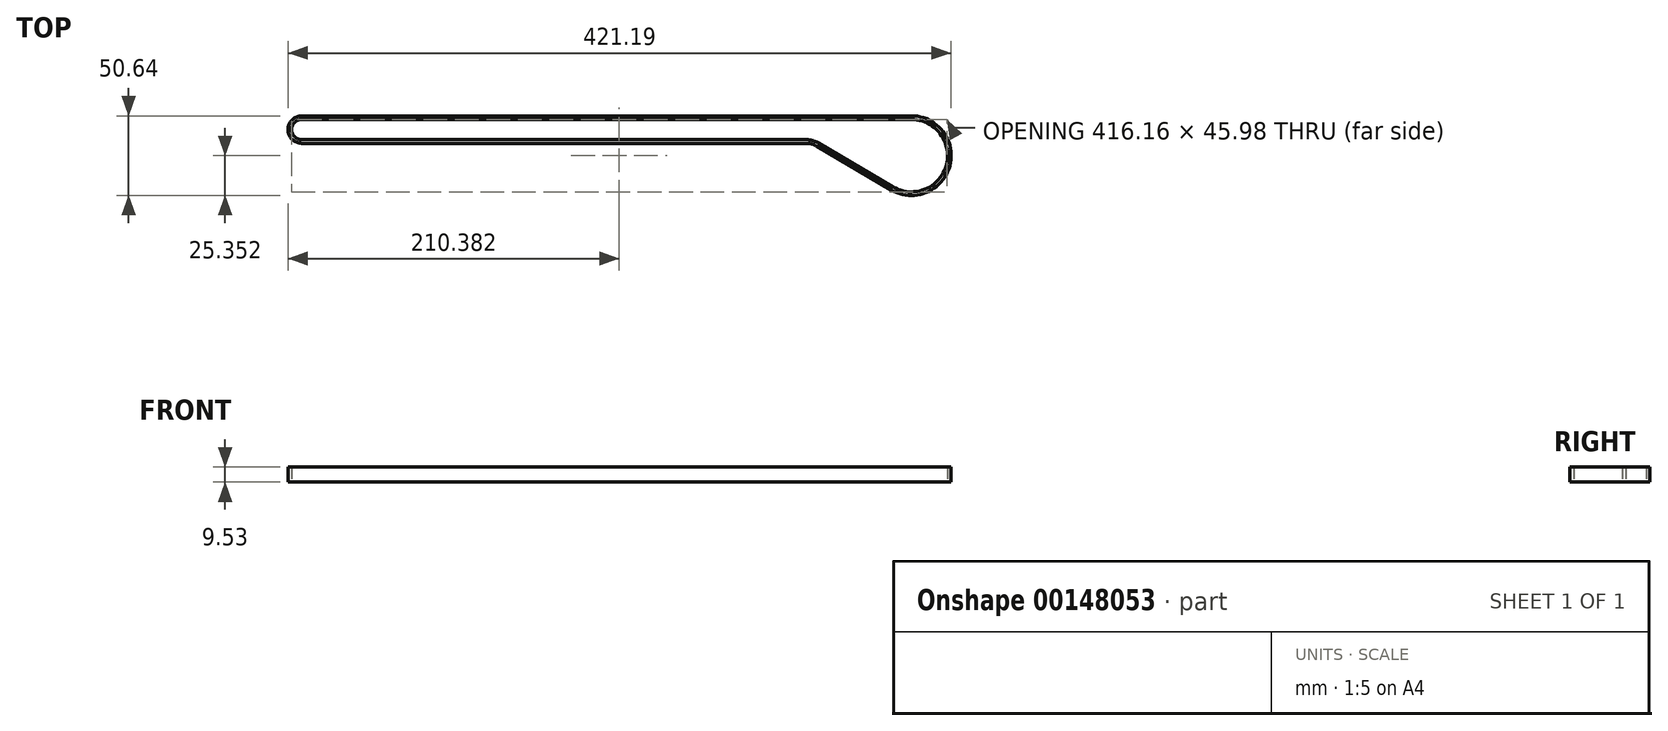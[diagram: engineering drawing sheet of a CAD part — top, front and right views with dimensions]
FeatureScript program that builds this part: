
annotation { "Feature Type Name" : "Feature", "Feature Type Description" : "" }
export const myFeature = defineFeature(function(context is Context, id is Id, definition is map)
    precondition{}
    {
        {
            var Q0;
            Q0=qCreatedBy(makeId("Top.planeOp"),FACE);
            var sketch = newSketch(context, id + "F0", { "sketchPlane" : qUnion([Q0])});
            skArc(sketch, "E0", {"start": v(-11.7, -42.85) * mm, "mid": v(22.2, -29.08) * mm, "end": v(0, 0) * mm});
            skLineSegment(sketch, "E1", {"start": v(0, 0) * mm, "end": v(-387.12, 0) * mm});
            skLineSegment(sketch, "E2", {"start": v(0, 0) * mm, "end": v(0, 2.3) * mm, "construction": true});
            skLineSegment(sketch, "E3", {"start": v(-387.12, 0) * mm, "end": v(-387.12, 2.3) * mm, "construction": true});
            skLineSegment(sketch, "E4", {"start": v(-387.12, 2.3) * mm, "end": v(0, 2.3) * mm});
            skLineSegment(sketch, "E5", {"start": v(-193.56, 0) * mm, "end": v(-193.56, -27.9) * mm, "construction": true});
            skLineSegment(sketch, "E6", {"start": v(-193.56, -27.9) * mm, "end": v(-66.56, -27.9) * mm, "construction": true});
            skArc(sketch, "E7", {"start": v(-60.1, -16.97) * mm, "mid": v(-63.21, -15.65) * mm, "end": v(-66.56, -15.2) * mm});
            skLineSegment(sketch, "E8", {"start": v(-66.56, -15.2) * mm, "end": v(-387.12, -15.2) * mm});
            skLineSegment(sketch, "E9", {"start": v(-66.56, -15.2) * mm, "end": v(-66.56, -12.9) * mm, "construction": true});
            skLineSegment(sketch, "E10", {"start": v(-387.12, -12.9) * mm, "end": v(-66.56, -12.9) * mm});
            skArc(sketch, "E11", {"start": v(-58.94, -14.99) * mm, "mid": v(-62.6, -13.44) * mm, "end": v(-66.56, -12.9) * mm});
            skArc(sketch, "E12", {"start": v(-12.86, -44.83) * mm, "mid": v(24.43, -29.68) * mm, "end": v(0, 2.3) * mm});
            skLineSegment(sketch, "E13", {"start": v(-58.94, -14.99) * mm, "end": v(-11.7, -42.85) * mm});
            skLineSegment(sketch, "E14", {"start": v(-60.1, -16.97) * mm, "end": v(-12.86, -44.83) * mm});
            skArc(sketch, "E15", {"start": v(-387.12, 2.3) * mm, "mid": v(-395.87, -6.45) * mm, "end": v(-387.12, -15.2) * mm});
            skArc(sketch, "E16", {"start": v(-387.12, 0) * mm, "mid": v(-393.57, -6.45) * mm, "end": v(-387.12, -12.9) * mm});
            skSolve(sketch);
        }
        {
            var Q0;
            Q0=qSketchRegion(id+"F0",true);
            extrude(context, id + "F1", {"entities" : qUnion([Q0]), "depth" : 9.52 * mm});
        }
    });
